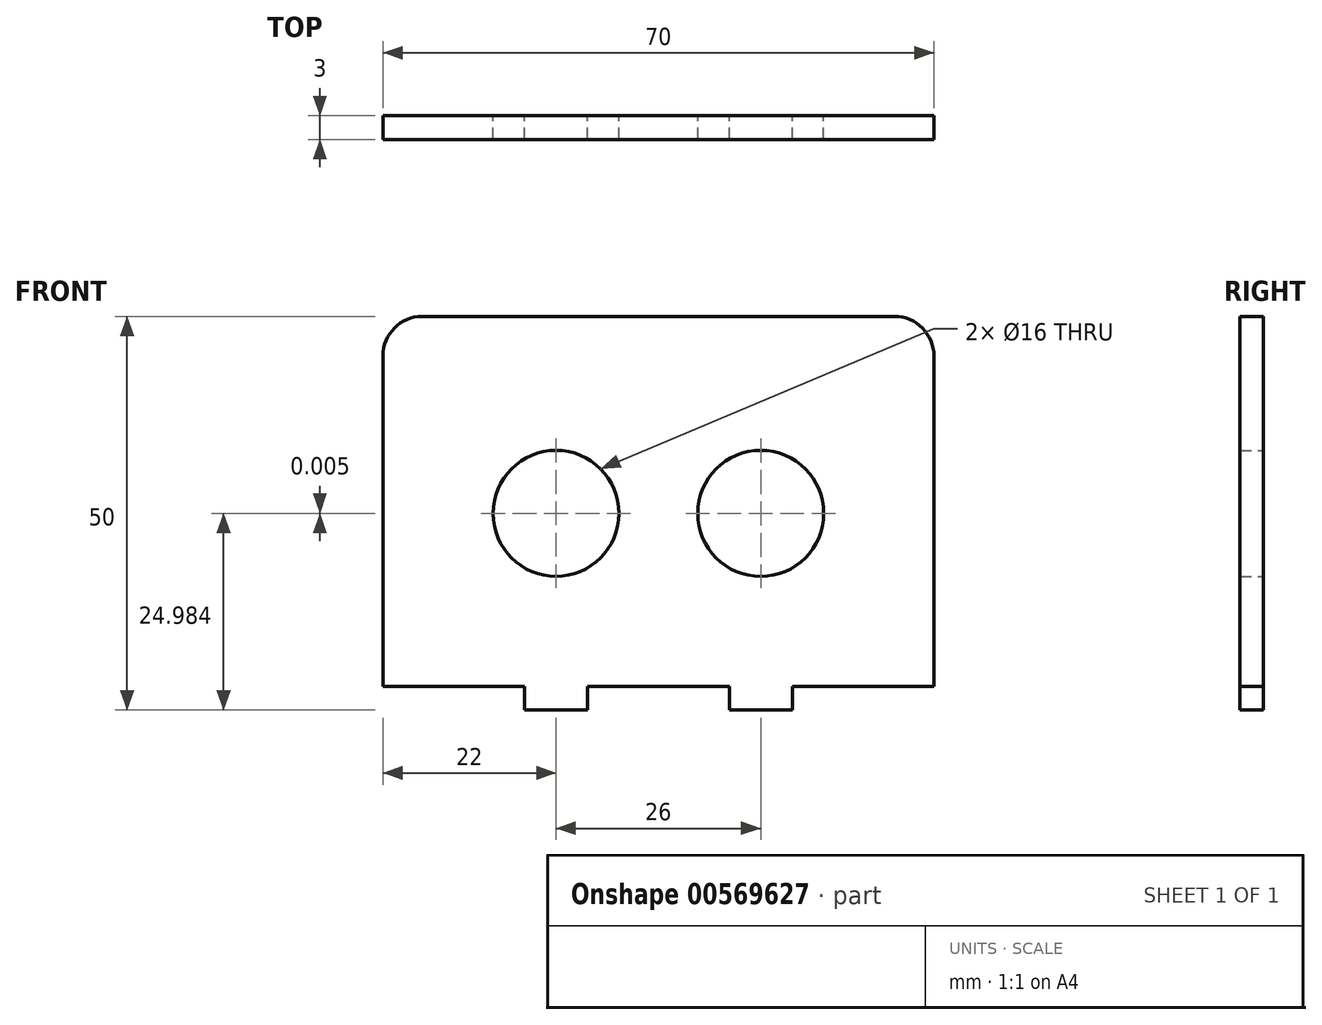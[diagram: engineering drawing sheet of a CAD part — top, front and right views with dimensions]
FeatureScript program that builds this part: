
annotation { "Feature Type Name" : "Feature", "Feature Type Description" : "" }
export const myFeature = defineFeature(function(context is Context, id is Id, definition is map)
    precondition{}
    {
        {
            var Q0;
            Q0=qCreatedBy(makeId("Front.planeOp"),FACE);
            var sketch = newSketch(context, id + "F0", { "sketchPlane" : qUnion([Q0])});
            skLineSegment(sketch, "E0.bottom", {"start": v(-30, 25) * mm, "end": v(30, 25) * mm});
            skLineSegment(sketch, "E0.top", {"start": v(-17, -25) * mm, "end": v(-9, -25) * mm});
            skLineSegment(sketch, "E0.left", {"start": v(-35, 20) * mm, "end": v(-35, -22) * mm});
            skLineSegment(sketch, "E0.right", {"start": v(35, 20) * mm, "end": v(35, -22) * mm});
            skLineSegment(sketch, "E1", {"start": v(-66.36, 0) * mm, "end": v(78.42, -0.03) * mm, "construction": true});
            skCircle(sketch, "E2", {"center": v(-13, -0.01) * mm, "radius": 8 * mm});
            skCircle(sketch, "E3", {"center": v(13, -0.02) * mm, "radius": 8 * mm});
            skLineSegment(sketch, "E4", {"start": v(-41.76, -22) * mm, "end": v(41.31, -22) * mm, "construction": true});
            skLineSegment(sketch, "E5", {"start": v(-35, -22) * mm, "end": v(-17, -22) * mm});
            skLineSegment(sketch, "E6", {"start": v(-17, -22) * mm, "end": v(-17, -25) * mm});
            skLineSegment(sketch, "E7", {"start": v(-9, -25) * mm, "end": v(-9, -22) * mm});
            skLineSegment(sketch, "E8", {"start": v(-9, -22) * mm, "end": v(9, -22) * mm});
            skLineSegment(sketch, "E9", {"start": v(9, -22) * mm, "end": v(9, -25) * mm});
            skLineSegment(sketch, "E10", {"start": v(9, -25) * mm, "end": v(17, -25) * mm});
            skLineSegment(sketch, "E11", {"start": v(17, -25) * mm, "end": v(17, -22) * mm});
            skLineSegment(sketch, "E12", {"start": v(17, -22) * mm, "end": v(35, -22) * mm});
            skPoint(sketch, "E13.visualSharp", {"position": v(-35, 25) * mm});
            skArc(sketch, "E13.filletArc", {"start": v(-30, 25) * mm, "mid": v(-33.54, 23.54) * mm, "end": v(-35, 20) * mm});
            skPoint(sketch, "E14.visualSharp", {"position": v(35, 25) * mm});
            skArc(sketch, "E14.filletArc", {"start": v(35, 20) * mm, "mid": v(33.54, 23.54) * mm, "end": v(30, 25) * mm});
            skSolve(sketch);
        }
        {
            var Q0;
            Q0=makeQuery(id+"F0.imprint","IMPRINT",FACE,{"disambiguationData":[TD([[makeQuery(id+"F0.imprint","IMPRINT",EDGE,{"derivedFrom":sQuery(id+"F0.wireOp",EDGE,"E0.bottom")}),-1.0]])]});
            extrude(context, id + "F1", {"entities" : qUnion([Q0]), "depth" : 3 * mm, "offsetDistance" : 25 * mm});
        }
    });
